# Revit family: Zumtobel ONLITE central CPS H
name_source: partatom
category: Electrical Equipment
revit_build: Autodesk Revit 2018 (Build: 20170223_1515(x64)
units: mm (PartAtom-declared; Revit-internal decimal feet)

## family parameters
Always vertical = No
Cut with Voids When Loaded = No
OmniClass Number = 23.80.10.00
OmniClass Title = Generation and Transformation Equipment
Panel Configuration = Two Columns, Circuits Across
Part Type = Panelboard
Room Calculation Point = No
Round Connector Dimension = Use Diameter
Shared = No
Work Plane-Based = Yes

## types (1)
- ONLITE central CPS H
    Default Elevation = 0 mm  [stored 0 ft]
    Height = 1800 mm
    Lamp = LED
    Length = 850 mm
    Manufacturer = Zumtobel Lighting
    Model = 22154690
    URL = http://www.zumtobel.com
    Width = 600 mm

note: [stored X ft] marks values corroborated as IEEE doubles in the binary element streams (Revit-internal decimal feet)

## geometry (parser evidence)
native form markers: Sweep x2
no freeform markers — native parametric forms only
